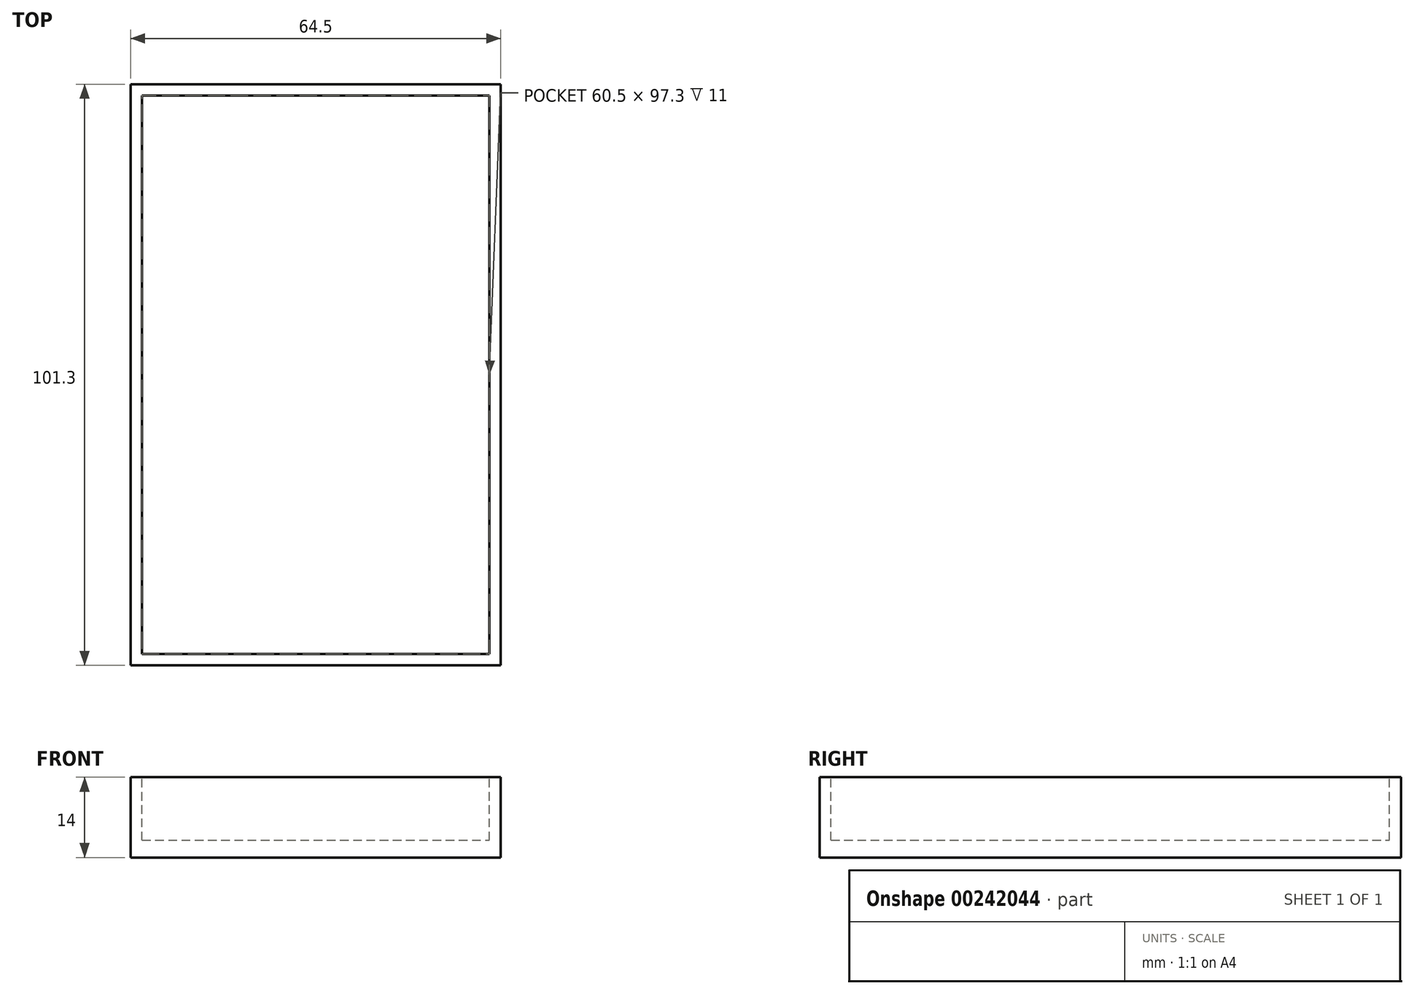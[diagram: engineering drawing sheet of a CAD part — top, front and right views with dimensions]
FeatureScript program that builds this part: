
annotation { "Feature Type Name" : "Feature", "Feature Type Description" : "" }
export const myFeature = defineFeature(function(context is Context, id is Id, definition is map)
    precondition{}
    {
        {
            var Q0;
            Q0=qCreatedBy(makeId("Top.planeOp"),FACE);
            var sketch = newSketch(context, id + "F0", { "sketchPlane" : qUnion([Q0])});
            skLineSegment(sketch, "E0.bottom", {"start": v(0, 0) * mm, "end": v(64.5, 0) * mm});
            skLineSegment(sketch, "E0.top", {"start": v(0, 101.3) * mm, "end": v(64.5, 101.3) * mm});
            skLineSegment(sketch, "E0.left", {"start": v(0, 0) * mm, "end": v(0, 101.3) * mm});
            skLineSegment(sketch, "E0.right", {"start": v(64.5, 0) * mm, "end": v(64.5, 101.3) * mm});
            skSolve(sketch);
        }
        {
            var Q0;
            Q0 = qSketchRegion(id + "F0", true);
            extrude(context, id + "F1", {"entities" : qUnion([Q0]), "depth" : 3 * mm});
        }
        {
            var Q0;
            Q0=makeQuery(id+"F1.opExtrude","CAP_FACE",FACE,{"disambiguationData":[OSD([sQuery(id+"F0.wireOp",EDGE,"E0.bottom"),sQuery(id+"F0.wireOp",EDGE,"E0.top"),sQuery(id+"F0.wireOp",EDGE,"E0.left"),sQuery(id+"F0.wireOp",EDGE,"E0.right")])],"isStart":false});
            extrude(context, id + "F2", {"entities" : qUnion([Q0]), "operationType" : NewBodyOperationType.ADD, "depth" : 11 * mm});
        }
        {
            var Q0;
            Q0=makeQuery(id+"F2.opExtrude","CAP_FACE",FACE,{"disambiguationData":[OSD([sQuery(id+"F0.wireOp",EDGE,"E0.bottom"),sQuery(id+"F0.wireOp",EDGE,"E0.top"),sQuery(id+"F0.wireOp",EDGE,"E0.left"),sQuery(id+"F0.wireOp",EDGE,"E0.right")])],"isStart":false});
            var sketch = newSketch(context, id + "F3", { "sketchPlane" : qUnion([Q0])});
            skLineSegment(sketch, "E1.bottom", {"start": v(2, 2) * mm, "end": v(62.5, 2) * mm});
            skLineSegment(sketch, "E1.top", {"start": v(2, 99.3) * mm, "end": v(62.5, 99.3) * mm});
            skLineSegment(sketch, "E1.left", {"start": v(2, 2) * mm, "end": v(2, 99.3) * mm});
            skLineSegment(sketch, "E1.right", {"start": v(62.5, 2) * mm, "end": v(62.5, 99.3) * mm});
            skSolve(sketch);
        }
        {
            var Q0;
            Q0 = qSketchRegion(id + "F3", true);
            extrude(context, id + "F4", {"entities" : qUnion([Q0]), "operationType" : NewBodyOperationType.REMOVE, "oppositeDirection" : true, "depth" : 11 * mm});
        }
    });
